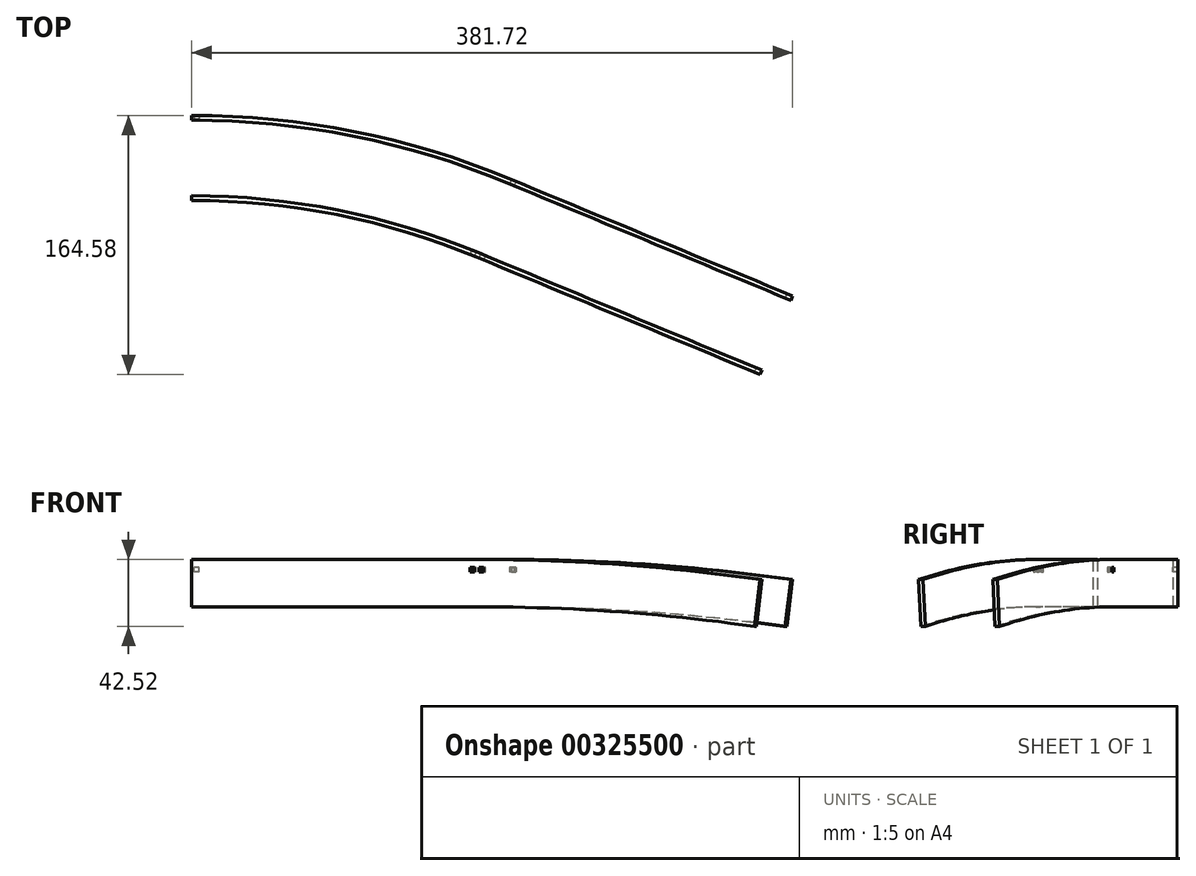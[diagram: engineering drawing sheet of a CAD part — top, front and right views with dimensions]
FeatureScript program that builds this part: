
annotation { "Feature Type Name" : "Feature", "Feature Type Description" : "" }
export const myFeature = defineFeature(function(context is Context, id is Id, definition is map)
    precondition{}
    {
        {
            var Q0;
            Q0=qCreatedBy(makeId("Top.planeOp"),FACE);
            var sketch = newSketch(context, id + "F0", { "sketchPlane" : qUnion([Q0])});
            skArc(sketch, "E0", {"start": v(0, 0) * mm, "mid": v(182.16, -36.23) * mm, "end": v(336.58, -139.42) * mm, "construction": true});
            skArc(sketch, "E1", {"start": v(0, 48) * mm, "mid": v(200.53, 8.11) * mm, "end": v(370.52, -105.48) * mm, "construction": true});
            skLineSegment(sketch, "E2", {"start": v(0, 48) * mm, "end": v(0, -476) * mm, "construction": true});
            skLineSegment(sketch, "E3", {"start": v(370.52, -105.48) * mm, "end": v(0, -476) * mm, "construction": true});
            skArc(sketch, "E4", {"start": v(0, 0) * mm, "mid": v(92.86, -9.15) * mm, "end": v(182.16, -36.23) * mm});
            skArc(sketch, "E5", {"start": v(0, 48) * mm, "mid": v(102.23, 37.93) * mm, "end": v(200.53, 8.11) * mm});
            skLineSegment(sketch, "E6", {"start": v(0, -476) * mm, "end": v(182.16, -36.23) * mm, "construction": true});
            skSolve(sketch);
        }
        {
            var Q0;
            Q0=qCreatedBy(makeId("Right.planeOp"),FACE);
            var sketch = newSketch(context, id + "F1", { "sketchPlane" : qUnion([Q0])});
            skLineSegment(sketch, "E7.bottom", {"start": v(-3, 5) * mm, "end": v(0, 5) * mm});
            skLineSegment(sketch, "E7.top", {"start": v(-3, -25) * mm, "end": v(0, -25) * mm});
            skLineSegment(sketch, "E7.left", {"start": v(-3, 5) * mm, "end": v(-3, -25) * mm});
            skLineSegment(sketch, "E7.right", {"start": v(0, 5) * mm, "end": v(0, -25) * mm});
            skLineSegment(sketch, "E8.bottom", {"start": v(51, 5) * mm, "end": v(48, 5) * mm});
            skLineSegment(sketch, "E8.top", {"start": v(51, -25) * mm, "end": v(48, -25) * mm});
            skLineSegment(sketch, "E8.left", {"start": v(51, 5) * mm, "end": v(51, -25) * mm});
            skLineSegment(sketch, "E8.right", {"start": v(48, 5) * mm, "end": v(48, -25) * mm});
            skSolve(sketch);
        }
        {
            var Q0;
            Q0 = qSketchRegion(id + "F1", true);
            var Q1;
            Q1=sQuery(id+"F0.wireOp",EDGE,"E4");
            sweep(context, id + "F2", {"profiles" : qUnion([Q0]), "path" : qUnion([Q1])});
        }
        {
            var Q0;
            Q0=qCreatedBy(makeId("Top.planeOp"),FACE);
            var sketch = newSketch(context, id + "F3", { "sketchPlane" : qUnion([Q0])});
            skArc(sketch, "E9.0", {"start": v(0, -3) * mm, "mid": v(92.28, -12.09) * mm, "end": v(181, -39) * mm, "construction": true});
            skLineSegment(sketch, "E10.0", {"start": v(0, 0) * mm, "end": v(0, -3) * mm, "construction": true});
            skArc(sketch, "E11.0", {"start": v(0, 0) * mm, "mid": v(92.86, -9.15) * mm, "end": v(182.16, -36.23) * mm, "construction": true});
            skArc(sketch, "E12", {"start": v(176.65, -37.22) * mm, "mid": v(178.1, -37.81) * mm, "end": v(179.56, -38.4) * mm});
            skArc(sketch, "E13", {"start": v(0, 0) * mm, "mid": v(90.54, -8.69) * mm, "end": v(177.77, -34.44) * mm});
            skArc(sketch, "E14", {"start": v(177.77, -34.44) * mm, "mid": v(179.23, -35.03) * mm, "end": v(180.7, -35.63) * mm});
            skLineSegment(sketch, "E15", {"start": v(177.77, -34.44) * mm, "end": v(176.65, -37.22) * mm});
            skLineSegment(sketch, "E16", {"start": v(180.7, -35.63) * mm, "end": v(179.56, -38.4) * mm});
            skArc(sketch, "E17", {"start": v(181, -39) * mm, "mid": v(180.28, -38.7) * mm, "end": v(179.56, -38.4) * mm, "construction": true});
            skSolve(sketch);
        }
        {
            var Q0;
            Q0 = qSketchRegion(id + "F3", true);
            extrude(context, id + "F4", {"entities" : qUnion([Q0]), "operationType" : NewBodyOperationType.REMOVE, "oppositeDirection" : true, "depth" : 3 * mm});
        }
        {
            var Q0;
            Q0=qCreatedBy(makeId("Front.planeOp"),FACE);
            var Q1;
            Q1=sQuery(id+"F0.wireOp",VERTEX,"E1.center");
            cPlane(context, id + "F5", {"entities" : qUnion([Q0, Q1]), "cplaneType" : CPlaneType.PLANE_POINT, "offset" : 25 * mm, "width" : 150 * mm, "height" : 150 * mm});
        }
        {
            var Q0;
            Q0=qCreatedBy(id+"F5.planeOp",FACE);
            var sketch = newSketch(context, id + "F6", { "sketchPlane" : qUnion([Q0])});
            skLineSegment(sketch, "E18", {"start": v(0, 0) * mm, "end": v(0, 46.52) * mm, "construction": true});
            skSolve(sketch);
        }
        {
            var Q0;
            Q0=qCreatedBy(makeId("Top.planeOp"),FACE);
            var sketch = newSketch(context, id + "F7", { "sketchPlane" : qUnion([Q0])});
            skArc(sketch, "E19.0", {"start": v(0, 48) * mm, "mid": v(200.53, 8.11) * mm, "end": v(370.52, -105.48) * mm, "construction": true});
            skLineSegment(sketch, "E19.1", {"start": v(0, 51) * mm, "end": v(0, 48) * mm, "construction": true});
            skArc(sketch, "E19.2", {"start": v(0, 51) * mm, "mid": v(102.81, 40.87) * mm, "end": v(201.67, 10.88) * mm, "construction": true});
            skArc(sketch, "E20", {"start": v(0, 48) * mm, "mid": v(0.79, 48) * mm, "end": v(1.57, 48) * mm});
            skArc(sketch, "E21", {"start": v(1.57, 48) * mm, "mid": v(3.14, 48) * mm, "end": v(4.71, 47.98) * mm});
            skArc(sketch, "E22", {"start": v(0, 51) * mm, "mid": v(0.79, 51) * mm, "end": v(1.58, 51) * mm});
            skArc(sketch, "E23", {"start": v(1.58, 51) * mm, "mid": v(3.16, 51) * mm, "end": v(4.74, 50.98) * mm});
            skLineSegment(sketch, "E24", {"start": v(1.58, 51) * mm, "end": v(1.57, 48) * mm});
            skLineSegment(sketch, "E25", {"start": v(4.74, 50.98) * mm, "end": v(4.71, 47.98) * mm});
            skSolve(sketch);
        }
        {
            var Q0;
            Q0 = qSketchRegion(id + "F7", true);
            extrude(context, id + "F8", {"entities" : qUnion([Q0]), "operationType" : NewBodyOperationType.REMOVE, "oppositeDirection" : true, "depth" : 3 * mm});
        }
        {
            var Q0;
            Q0=sQuery(id+"F0.wireOp",EDGE,"E6");
            var Q1;
            Q1=sQuery(id+"F0.wireOp",VERTEX,"E4.end");
            cPlane(context, id + "F9", {"entities" : qUnion([Q0, Q1]), "cplaneType" : CPlaneType.LINE_POINT, "offset" : 25 * mm, "width" : 150 * mm, "height" : 150 * mm});
        }
        {
            var Q0;
            Q0=qCreatedBy(id+"F9.planeOp",FACE);
            var sketch = newSketch(context, id + "F10", { "sketchPlane" : qUnion([Q0])});
            skCircle(sketch, "E26", {"center": v(-182.16, -1488) * mm, "radius": 1488 * mm, "construction": true});
            skPoint(sketch, "E27", {"position": v(-182.16, 0) * mm});
            skLineSegment(sketch, "E28", {"start": v(-182.16, 0) * mm, "end": v(-182.16, -1488) * mm, "construction": true});
            skArc(sketch, "E29", {"start": v(-182.16, 0) * mm, "mid": v(-376.38, -12.73) * mm, "end": v(-567.28, -50.7) * mm, "construction": true});
            skLineSegment(sketch, "E30", {"start": v(-567.28, -50.7) * mm, "end": v(-182.16, -1488) * mm, "construction": true});
            skArc(sketch, "E31", {"start": v(-182.16, 0) * mm, "mid": v(-279.48, -3.19) * mm, "end": v(-376.38, -12.73) * mm});
            skSolve(sketch);
        }
        {
            var Q0;
            {var subQ0=sQuery(id+"F1.wireOp",EDGE,"E7.top");var subQ1=sQuery(id+"F0.wireOp",EDGE,"E1");var subQ2=sQuery(id+"F1.wireOp",EDGE,"E7.left");var subQ3=sQuery(id+"F1.wireOp",EDGE,"E7.right");Q0=makeQuery(id+"FrGcrS4mNiOU0hm_2.29.F4.boolean.opBoolean","SPLIT",FACE,{"disambiguationData":[TD([makeQuery(id+"F2.opSweep","SWEPT_FACE",FACE,{"disambiguationData":[OSD([subQ1,subQ0])]})])],"derivedFrom":makeQuery(id+"F2.opSweep","CAP_FACE",FACE,{"disambiguationData":[OSD([sQuery(id+"F0.wireOp",VERTEX,"E1.end"),sQuery(id+"F1.wireOp",EDGE,"E7.bottom"),subQ0,subQ2,subQ3])],"isStart":false})});}
            var sketch = newSketch(context, id + "F11", { "sketchPlane" : qUnion([Q0])});
            skLineSegment(sketch, "E32.bottom", {"start": v(36.23, 5) * mm, "end": v(33.23, 5) * mm});
            skLineSegment(sketch, "E32.top", {"start": v(36.23, -25) * mm, "end": v(33.23, -25) * mm});
            skLineSegment(sketch, "E32.left", {"start": v(36.23, 5) * mm, "end": v(36.23, -25) * mm});
            skLineSegment(sketch, "E32.right", {"start": v(33.23, 5) * mm, "end": v(33.23, -25) * mm});
            skLineSegment(sketch, "E33.bottom", {"start": v(87.23, 5) * mm, "end": v(84.23, 5) * mm});
            skLineSegment(sketch, "E33.top", {"start": v(87.23, -25) * mm, "end": v(84.23, -25) * mm});
            skLineSegment(sketch, "E33.left", {"start": v(87.23, 5) * mm, "end": v(87.23, -25) * mm});
            skLineSegment(sketch, "E33.right", {"start": v(84.23, 5) * mm, "end": v(84.23, -25) * mm});
            skSolve(sketch);
        }
        {
            var Q0;
            Q0 = qSketchRegion(id + "F10", true);
            var Q1;
            Q1 = qSketchRegion(id + "F11", true);
            var Q2;
            Q2=sQuery(id+"F10.wireOp",EDGE,"E31");
            sweep(context, id + "F12", {"operationType" : NewBodyOperationType.ADD, "profiles" : qUnion([Q0, Q1]), "path" : qUnion([Q2])});
        }
        {
            var Q0;
            Q0=makeQuery(id+"F12.opSweep","SWEPT_FACE",FACE,{"disambiguationData":[OSD([sQuery(id+"F10.wireOp",EDGE,"Zbys7VEU-cKmb-QWgB-M3Ah-95dSQQJA0nD2"),sQuery(id+"F11.wireOp",EDGE,"E32.right")])]});
            var sketch = newSketch(context, id + "F13", { "sketchPlane" : qUnion([Q0])});
            skLineSegment(sketch, "E34.0", {"start": v(180.59, -3) * mm, "end": v(180.59, 0) * mm, "construction": true});
            skLineSegment(sketch, "E35.0", {"start": v(177.47, 0) * mm, "end": v(180.63, 0) * mm, "construction": true});
            skLineSegment(sketch, "E35.1", {"start": v(177.45, 0) * mm, "end": v(180.59, 0) * mm, "construction": true});
            skLineSegment(sketch, "E36.0", {"start": v(177.45, -3) * mm, "end": v(177.45, 0) * mm, "construction": true});
            skLineSegment(sketch, "E37.0", {"start": v(177.45, -3) * mm, "end": v(180.59, -3) * mm, "construction": true});
            skLineSegment(sketch, "E38", {"start": v(180.59, -1.5) * mm, "end": v(182.16, -1.5) * mm, "construction": true});
            skArc(sketch, "E39", {"start": v(182.16, -1.5) * mm, "mid": v(182.94, -1.5) * mm, "end": v(183.73, -1.5) * mm, "construction": true});
            skArc(sketch, "E40", {"start": v(183.73, -1.5) * mm, "mid": v(185.3, -1.5) * mm, "end": v(186.87, -1.5) * mm, "construction": true});
            skArc(sketch, "E41", {"start": v(183.73, 0) * mm, "mid": v(185.3, 0) * mm, "end": v(186.87, 0) * mm});
            skArc(sketch, "E42", {"start": v(183.73, -3) * mm, "mid": v(185.3, -3) * mm, "end": v(186.86, -3) * mm});
            skLineSegment(sketch, "E43", {"start": v(183.73, 0) * mm, "end": v(183.73, -3) * mm});
            skLineSegment(sketch, "E44", {"start": v(186.87, 0) * mm, "end": v(186.86, -3) * mm});
            skSolve(sketch);
        }
        {
            var Q0;
            Q0 = qSketchRegion(id + "F13", true);
            var Q1;
            Q1=makeQuery(id+"F12.opSweep","SWEPT_FACE",FACE,{"disambiguationData":[OSD([sQuery(id+"F10.wireOp",EDGE,"Zbys7VEU-cKmb-QWgB-M3Ah-95dSQQJA0nD2"),sQuery(id+"F11.wireOp",EDGE,"E33.left")])]});
            extrude(context, id + "F14", {"entities" : qUnion([Q0]), "operationType" : NewBodyOperationType.REMOVE, "endBound" : BoundingType.UP_TO_SURFACE, "oppositeDirection" : true, "endBoundEntityFace" : qUnion([Q1]), "depth" : 25 * mm});
        }
        {
            var Q0;
            Q0=qCreatedBy(makeId("Top.planeOp"),FACE);
            var Q1;
            Q1=sQuery(id+"F10.wireOp",VERTEX,"E28.end");
            cPlane(context, id + "F15", {"entities" : qUnion([Q0, Q1]), "cplaneType" : CPlaneType.PLANE_POINT, "offset" : 25 * mm, "width" : 150 * mm, "height" : 150 * mm});
        }
        {
            var Q0;
            Q0=qCreatedBy(id+"F15.planeOp",FACE);
            var sketch = newSketch(context, id + "F16", { "sketchPlane" : qUnion([Q0])});
            skLineSegment(sketch, "E45", {"start": v(182.16, -36.23) * mm, "end": v(161.15, -86.94) * mm, "construction": true});
            skSolve(sketch);
        }
    });
